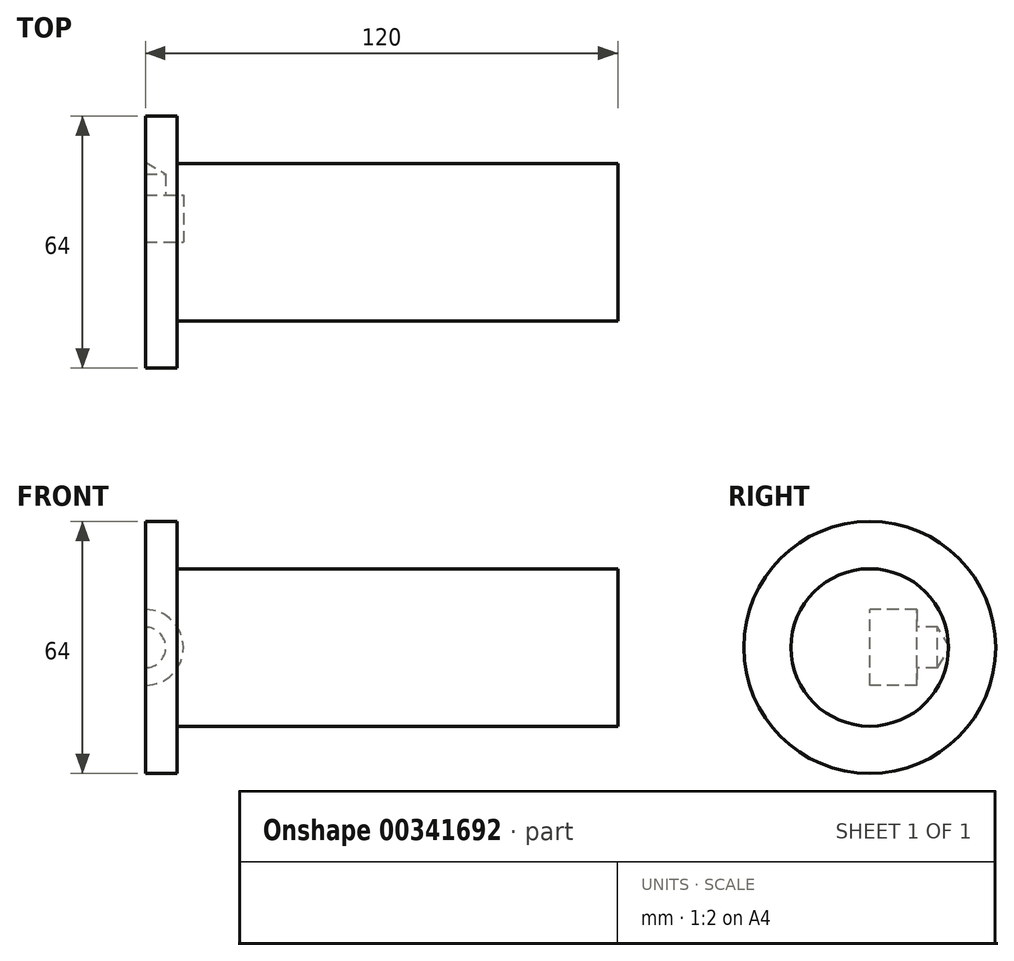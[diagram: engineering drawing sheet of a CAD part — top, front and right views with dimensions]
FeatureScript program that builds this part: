
annotation { "Feature Type Name" : "Feature", "Feature Type Description" : "" }
export const myFeature = defineFeature(function(context is Context, id is Id, definition is map)
    precondition{}
    {
        {
            var Q0;
            Q0=qCreatedBy(makeId("Front.planeOp"),FACE);
            var sketch = newSketch(context, id + "F0", { "sketchPlane" : qUnion([Q0])});
            skLineSegment(sketch, "E0", {"start": v(0, 32) * mm, "end": v(8, 32) * mm});
            skLineSegment(sketch, "E1", {"start": v(8, 32) * mm, "end": v(8, 20) * mm});
            skLineSegment(sketch, "E2", {"start": v(8, 20) * mm, "end": v(120, 20) * mm});
            skLineSegment(sketch, "E3", {"start": v(120, 20) * mm, "end": v(120, 0) * mm});
            skLineSegment(sketch, "E4", {"start": v(120, 0) * mm, "end": v(0, 0) * mm});
            skLineSegment(sketch, "E5", {"start": v(0, 0) * mm, "end": v(0, 32) * mm});
            skSolve(sketch);
        }
        {
            var Q0;
            Q0=makeQuery(id+"F0.imprint","IMPRINT",FACE,{"disambiguationData":[TD([[makeQuery(id+"F0.imprint","IMPRINT",EDGE,{"derivedFrom":sQuery(id+"F0.wireOp",EDGE,"E0")}),-1.0]])]});
            var Q1;
            Q1=sQuery(id+"F0.wireOp",EDGE,"E4");
            revolve(context, id + "F1", {"entities" : qUnion([Q0]), "axis" : qUnion([Q1]), "revolveType" : RevolveType.FULL});
        }
        {
            var Q0;
            Q0=sQuery(id+"F0.wireOp",VERTEX,"E5.start");
            var Q1;
            Q1=makeQuery(id+"F1.opRevolve","SWEPT_BODY",BODY,{"disambiguationData":[OSD([sQuery(id+"F0.wireOp",EDGE,"E0"),sQuery(id+"F0.wireOp",EDGE,"E1"),sQuery(id+"F0.wireOp",EDGE,"E2"),sQuery(id+"F0.wireOp",EDGE,"E3"),sQuery(id+"F0.wireOp",EDGE,"E4"),sQuery(id+"F0.wireOp",EDGE,"E5")])]});
            hole(context, id + "F2", {"style" : HoleStyle.C_BORE, "endStyle" : HoleEndStyle.BLIND, "standardTappedOrClearance" : lookupTablePath({ "standard" : "ISO", "fit" : "Normal", "engagement" : "75%", "pitch" : "1.75 mm", "size" : "M12", "type" : "Tapped" }), "standardBlindInLast" : lookupTablePath({ "fit" : "Standard", "standard" : "ISO", "engagement" : "75%", "pitch" : "1.75 mm", "size" : "M12", "type" : "Tapped" }), "holeDiameter" : 10.3 * mm, "cBoreDiameter" : 19.25 * mm, "cBoreDepth" : 12 * mm, "showTappedDepth" : true, "holeDepth" : 17.25 * mm, "isTappedThrough" : true, "tappedDepth" : 12 * mm, "tapClearance" : 3, "locations" : qUnion([Q0]), "scope" : qUnion([Q1]), "majorDiameter" : 12 * mm});
        }
    });
